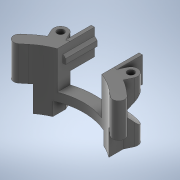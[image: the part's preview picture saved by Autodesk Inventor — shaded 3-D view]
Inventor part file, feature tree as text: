
AUTODESK INVENTOR PART (.ipt)
format: ipt  version: 2020 (Build 240168000, 168)  size: 576,512 bytes
history: native  units: mm
features: sketch x10, extrude x9, projected_geometry x7, other x2, sweep x1
ambient origin geometry x8: Origin, YZ Plane, XZ Plane, XY Plane, X Axis, Y Axis, Z Axis, Center Point
bodies: Body1 (feature_tree)
feature tree (29):
  other  "Твердое тело1"
  extrude  "Выдавливание1"  Depth=35.0mm TaperAngle=0.0deg
  sketch  "Эскиз2"
  extrude  "Выдавливание2"  Depth=4.0mm
  sweep  "Сдвиг1"
  extrude  "Выдавливание5"  Depth=8.0mm
  extrude  "Выдавливание6"  Depth=35.0mm TaperAngle=0.0deg
  extrude  "Выдавливание7"  Depth=8.5mm
  extrude  "Выдавливание8"  TaperAngle=45.0deg  [1 undecoded]
  other  "РабПлоскость1"
  extrude  "Выдавливание9"  Depth=8.5mm
  extrude  "Выдавливание10"  TaperAngle=45.0deg  [1 undecoded]
  extrude  "Выдавливание11"  TaperAngle=0.0deg  [1 undecoded]
  sketch  "Эскиз1"
  sketch  "Эскиз3"
  projected_geometry  "Спроецированная петля1"
  projected_geometry  "Спроецированная петля2"
  sketch  "3D эскиз1"
  sketch  "Эскиз4"
  sketch  "Эскиз6"
  projected_geometry  "Спроецированная петля4"
  sketch  "Эскиз7"
  projected_geometry  "Спроецированная петля5"
  sketch  "Эскиз9"
  projected_geometry  "Спроецированная петля7"
  sketch  "Эскиз11"
  projected_geometry  "Спроецированная петля8"
  sketch  "Эскиз12"
  projected_geometry  "Спроецированная петля9"
note: 3 required parameter values undecoded (feature->parameter linkage not recoverable at this tier; creation-order binding heuristic only, values carry confidence <= 0.55)
